# Revit family: Domotics-SerieCivili-GEWISS-27COMBI_SYSTEM-IP55_PRESA_ITA
name_source: partatom
category: Apparecchi elettrici
revit_build: Autodesk Revit 2016 (Build: 20161004_0715(x64)
units: mm (PartAtom-declared; Revit-internal decimal feet)

## family parameters
Condiviso = Sì
Host = Superficie
Mantenere orientamento annotazione = Sì
Numero OmniClass = 23.80.50.14
Punto di calcolo locali = No
Quota connettore circolare = Usa diametro
Taglio con vuoti quando caricato = Sì
Tipo di parte = Normale
Titolo OmniClass = Plug Connectors

## types (1)
- Domotics-SerieCivili-GEWISS-27COMBI_SYSTEM-IP55_PRESA_ITA
    Caratteristiche = Standard Italiano
    Catalogo = DOMOTICS
    Catalogo Serie = 27COMBI
    Classe isolamento = II
    Codice EAN = 8011564095465
    Codice Electrocod = 0131
    Colore = Grigio RAL 7035
    Colore portella = Trasparente
    Coppia serraggio viti = 0,8NM
    Descrizione = PRESA STD ITA.2P+T 16A BIV.STAGNA
    Descrizione: = Presa 2P+T - 16 A bivalente
    Dim. esterne BxHxP (mm) = 66x82x65
    GW - Testo elettrico = 10/16
    Glow Wire Test = 650°C
    Grado di protezione = IP55
    IDF = 19c93e40-1a99-46aa-9b32-a5c1b16e1856
    IDT = a9e83055-bc3d-4fd1-a2af-8daed6b86314
    Immagine tipo = GW27841.jpg
    Modello = GW27841
    N. fori Ã˜ 23 con passacavo = 1
    N. fori Ã˜ 23 sfondabili: = Laterali 3 / Sul fondo 1
    Norma di riferimento = Italiano
    Norma di riferimento: = IEC 60884-1
    Offset = 0 mm  [stored 0 ft]
    Produttore = GEWISS S.p.A.
    Prospetto di default = 1219 mm
    SEO = Contenitore
    Scheda Tecnica = https://www.gewiss.com
    Temperatura di installazione = -25 +60 °C
    Tensione = 230 V ac
    Tensione: = 250 V ac
    Termopressione con biglia = 70 °C
    Tipo = Presa 2P+T - 16 A bivalente
    Tipo portella = Con membrana
    Tipo sfondabili = Asportabili con utensile
    URL = https://www.gewiss.com
    Versione file RFA = 19.4
    Viti coperchio = Acciaio inox

note: [stored X ft] marks values corroborated as IEEE doubles in the binary element streams (Revit-internal decimal feet)

## geometry (parser evidence)
native form markers: Sweep x2
no freeform markers — native parametric forms only
